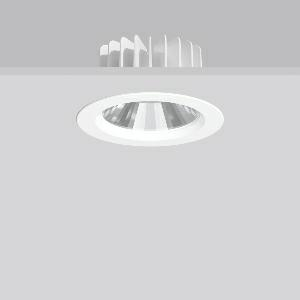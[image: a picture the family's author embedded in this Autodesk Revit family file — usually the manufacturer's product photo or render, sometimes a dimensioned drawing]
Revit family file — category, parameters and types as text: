
# Revit family: ledona_round_ip65_901797_002_1_51aa
name_source: partatom
category: Lighting Fixtures
units: mm (PartAtom-declared; Revit-internal decimal feet)

## family parameters
Cut with Voids When Loaded = No
Host = Face
Light Source = No
Part Type = Normal
Room Calculation Point = No
Round Connector Dimension = Use Diameter
Shared = No

## types (1)
- MultiLumen 1 (1 x LED Modul 940, 1650 lm, 4000)
    Apparent Load = 12 VA
    Approval mark = CE
    CIE Flux Codes = 89 99 100 100 100
    Color Rendering = 92
    Color Temperature = 4000
    Default Elevation = 1800 mm
    Height = 0 mm  [stored 0 ft]
    Lamp = 1 x LED Modul 940
    Lamp Light Flux = 1650 lm
    Lamp count = 1
    Length = 180 mm  [stored 0.590551 ft]
    Lifetime = 50000 h
    Luminous efficacy = 138 lm/W
    Manufacturer = RZB
    ModVariant = No
    Model = 901797.002.1
    Mounting Place = Ceiling
    Mounting Type = Recessed
    Number of Poles = 1
    OnlyDefault = Yes
    Power Factor = 1
    Product Name = LEDONA round IP65
    Product group = Recessed downlights
    ProductGroupID = 402
    Protection Class = Protection class II
    Protection Degree = IP 65
    RLX_Detail_Level = 1
    RLX_Emergency_Light_Flux = 0 lm
    RLX_Emergency_Type = 0
    RLX_Emergency_Type_DB = No
    RlxData = <blob elided: 38409 chars, md5=5ac6b086>
    Socket = socket
    Standby Power = 0 W
    System Light Flux = 1650 lm
    System Power = 12 W
    Type Comments = MultiLumen 1
    Type Image = 901346.002.jpg
    URL = http://relux.com
    VarID = multilumen_1
    Voltage = 230 V
    Voltage Range = 220-240 V
    Weight = 0.00 kg
    Width = 0 mm  [stored 0 ft]

note: [stored X ft] marks values corroborated as IEEE doubles in the binary element streams (Revit-internal decimal feet)

## geometry (parser evidence)
native form markers: Blend x4, Sweep x9
no freeform markers — native parametric forms only
